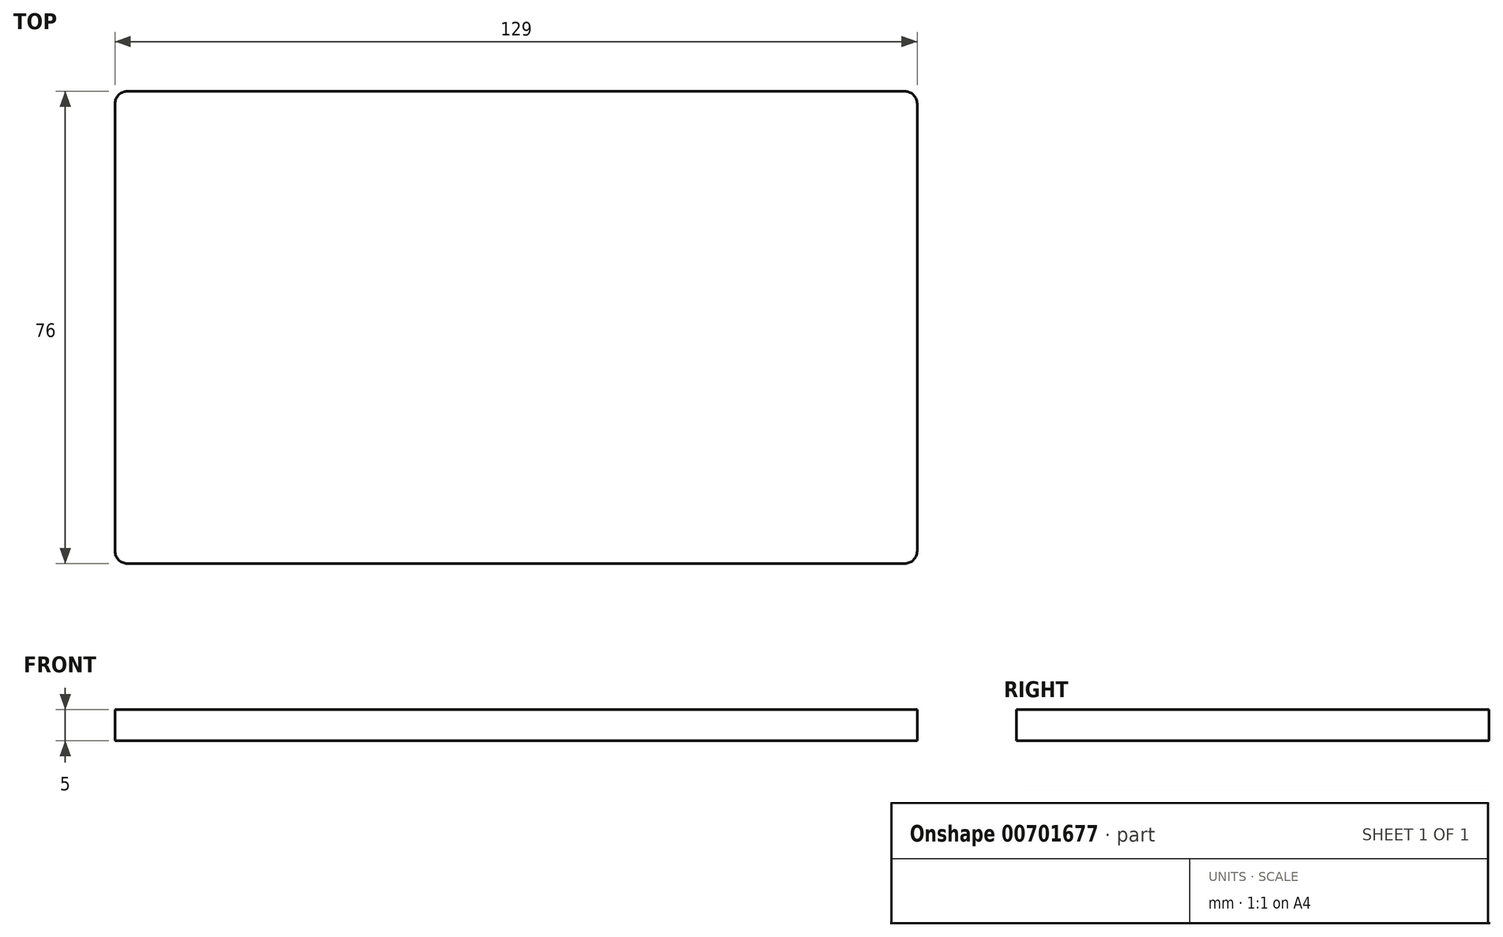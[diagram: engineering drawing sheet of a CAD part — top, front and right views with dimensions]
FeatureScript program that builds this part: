
annotation { "Feature Type Name" : "Feature", "Feature Type Description" : "" }
export const myFeature = defineFeature(function(context is Context, id is Id, definition is map)
    precondition{}
    {
        {
            var Q0;
            Q0=qCreatedBy(makeId("Top.planeOp"),FACE);
            var sketch = newSketch(context, id + "F0", { "sketchPlane" : qUnion([Q0]), "disableImprinting" : false});
            skLineSegment(sketch, "E0.bottom", {"start": v(-62.5, 38) * mm, "end": v(62.5, 38) * mm});
            skLineSegment(sketch, "E0.top", {"start": v(-62.5, -38) * mm, "end": v(62.5, -38) * mm});
            skLineSegment(sketch, "E0.left", {"start": v(-64.5, 36) * mm, "end": v(-64.5, -36) * mm});
            skLineSegment(sketch, "E0.right", {"start": v(64.5, 36) * mm, "end": v(64.5, -36) * mm});
            skPoint(sketch, "E0.middle", {"position": v(0, 0) * mm});
            skPoint(sketch, "E1.visualSharp", {"position": v(-64.5, 38) * mm});
            skArc(sketch, "E1.filletArc", {"start": v(-62.5, 38) * mm, "mid": v(-63.91, 37.41) * mm, "end": v(-64.5, 36) * mm});
            skPoint(sketch, "E2.visualSharp", {"position": v(64.5, 38) * mm});
            skArc(sketch, "E2.filletArc", {"start": v(64.5, 36) * mm, "mid": v(63.91, 37.41) * mm, "end": v(62.5, 38) * mm});
            skPoint(sketch, "E3.visualSharp", {"position": v(-64.5, -38) * mm});
            skArc(sketch, "E3.filletArc", {"start": v(-64.5, -36) * mm, "mid": v(-63.91, -37.41) * mm, "end": v(-62.5, -38) * mm});
            skPoint(sketch, "E4.visualSharp", {"position": v(64.5, -38) * mm});
            skArc(sketch, "E4.filletArc", {"start": v(62.5, -38) * mm, "mid": v(63.91, -37.41) * mm, "end": v(64.5, -36) * mm});
            skSolve(sketch);
        }
        {
            var Q0;
            Q0=makeQuery(id+"F0.imprint","IMPRINT",FACE,{"disambiguationData":[TD([[makeQuery(id+"F0.imprint","IMPRINT",EDGE,{"derivedFrom":sQuery(id+"F0.wireOp",EDGE,"E0.bottom")}),-1.0]])]});
            extrude(context, id + "F1", {"entities" : qUnion([Q0]), "depth" : 5 * mm, "offsetDistance" : 25 * mm});
        }
    });
